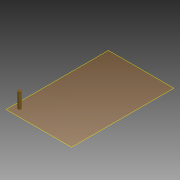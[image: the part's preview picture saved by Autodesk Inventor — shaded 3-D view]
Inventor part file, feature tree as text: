
AUTODESK INVENTOR PART (.ipt)
format: ipt  version: 2013 SP2 (Build 170200200, 200)  size: 77,312 bytes
history: native  units: mm
features: extrude x2, sketch x2, plane x1, reference x1
ambient origin geometry x8: Origin, YZ Plane, XZ Plane, XY Plane, X Axis, Y Axis, Z Axis, Center Point
bodies: Solid1 (feature_tree)
feature tree (6):
  plane  "Work Plane1"
  extrude  "Extrusion1"  Depth=3.0mm
  extrude  "Extrusion2"  [1 undecoded]
  sketch  "Sketch1"  dims[d0=16.5mm d1=0.0mm d2=3.0mm]
  reference  "Reference1"
  sketch  "Sketch2"  dims[d3=6.0mm d4=0.0mm]
note: 1 required parameter value undecoded (feature->parameter linkage not recoverable at this tier; creation-order binding heuristic only, values carry confidence <= 0.55)
